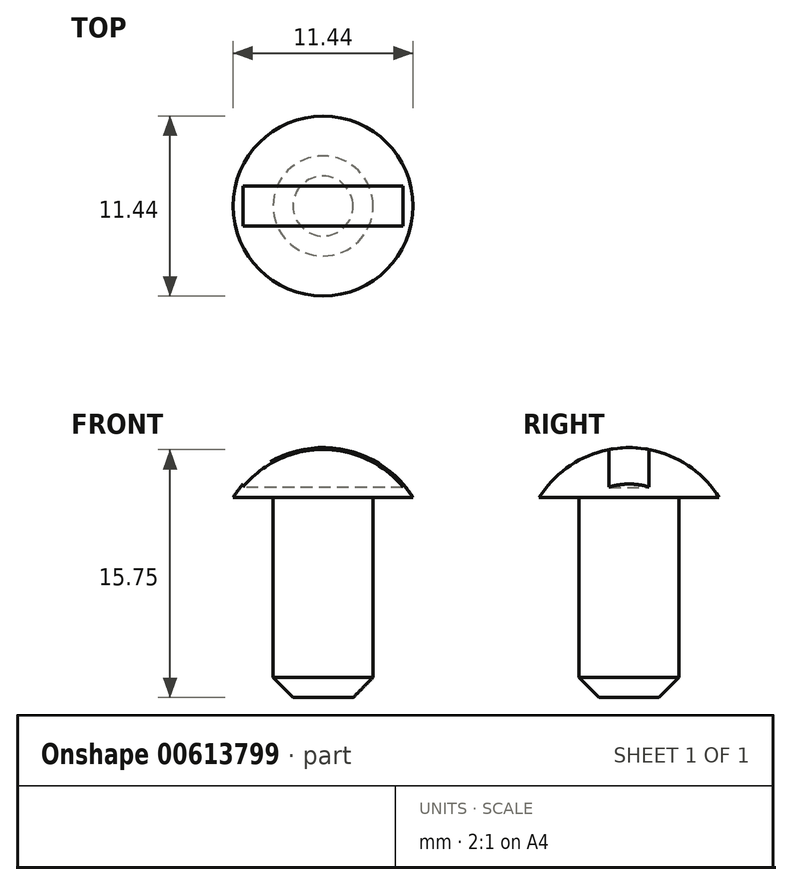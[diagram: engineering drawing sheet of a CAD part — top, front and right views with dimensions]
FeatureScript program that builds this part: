
annotation { "Feature Type Name" : "Feature", "Feature Type Description" : "" }
export const myFeature = defineFeature(function(context is Context, id is Id, definition is map)
    precondition{}
    {
        {
            var Q0;
            Q0=qCreatedBy(makeId("Front.planeOp"),FACE);
            var sketch = newSketch(context, id + "F0", { "sketchPlane" : qUnion([Q0])});
            skLineSegment(sketch, "E0", {"start": v(0, 0) * mm, "end": v(3.18, 0) * mm});
            skLineSegment(sketch, "E1", {"start": v(3.18, 0) * mm, "end": v(3.18, 12.7) * mm});
            skLineSegment(sketch, "E2", {"start": v(3.18, 12.7) * mm, "end": v(5.72, 12.7) * mm});
            skArc(sketch, "E3", {"start": v(0, 15.88) * mm, "mid": v(3.27, 15.03) * mm, "end": v(5.72, 12.7) * mm});
            skPoint(sketch, "E4.start.orphan", {"position": v(0, 10.48) * mm});
            skLineSegment(sketch, "E5", {"start": v(0, 15.88) * mm, "end": v(0, 0) * mm});
            skSolve(sketch);
        }
        {
            var Q0;
            Q0=makeQuery(id+"F0.imprint","IMPRINT",FACE,{"disambiguationData":[TD([[makeQuery(id+"F0.imprint","IMPRINT",EDGE,{"derivedFrom":sQuery(id+"F0.wireOp",EDGE,"E0")}),1.0]])]});
            var Q1;
            Q1=sQuery(id+"F0.wireOp",EDGE,"E5");
            revolve(context, id + "F1", {"entities" : qUnion([Q0]), "axis" : qUnion([Q1]), "revolveType" : RevolveType.FULL});
        }
        {
            var Q0;
            Q0=makeQuery(id+"F1.opRevolve","SWEPT_FACE",FACE,{"disambiguationData":[OSD([sQuery(id+"F0.wireOp",EDGE,"E0")])]});
            chamfer(context, id + "F2", {"entities" : qUnion([Q0]), "width" : 1.27 * mm, "tangentPropagation" : true});
        }
        {
            var Q0;
            Q0=makeQuery(id+"F1.opRevolve","SWEPT_FACE",FACE,{"disambiguationData":[OSD([sQuery(id+"F0.wireOp",EDGE,"E2")])]});
            cPlane(context, id + "F3", {"entities" : qUnion([Q0]), "cplaneType" : CPlaneType.OFFSET, "offset" : 0.64 * mm, "oppositeDirection" : true, "width" : 152.4 * mm, "height" : 152.4 * mm});
        }
        {
            var Q0;
            Q0=qCreatedBy(id+"F3.planeOp",FACE);
            var sketch = newSketch(context, id + "F4", { "sketchPlane" : qUnion([Q0])});
            skLineSegment(sketch, "E6.bottom", {"start": v(5.08, 1.27) * mm, "end": v(-5.08, 1.27) * mm});
            skLineSegment(sketch, "E6.top", {"start": v(5.08, -1.27) * mm, "end": v(-5.08, -1.27) * mm});
            skLineSegment(sketch, "E6.left", {"start": v(5.08, 1.27) * mm, "end": v(5.08, -1.27) * mm});
            skLineSegment(sketch, "E6.right", {"start": v(-5.08, 1.27) * mm, "end": v(-5.08, -1.27) * mm});
            skPoint(sketch, "E6.middle", {"position": v(0, 0) * mm});
            skSolve(sketch);
        }
        {
            var Q0;
            Q0 = qSketchRegion(id + "F4", true);
            extrude(context, id + "F5", {"entities" : qUnion([Q0]), "operationType" : NewBodyOperationType.REMOVE, "oppositeDirection" : true, "depth" : 25.4 * mm, "offsetDistance" : 25.4 * mm});
        }
    });
